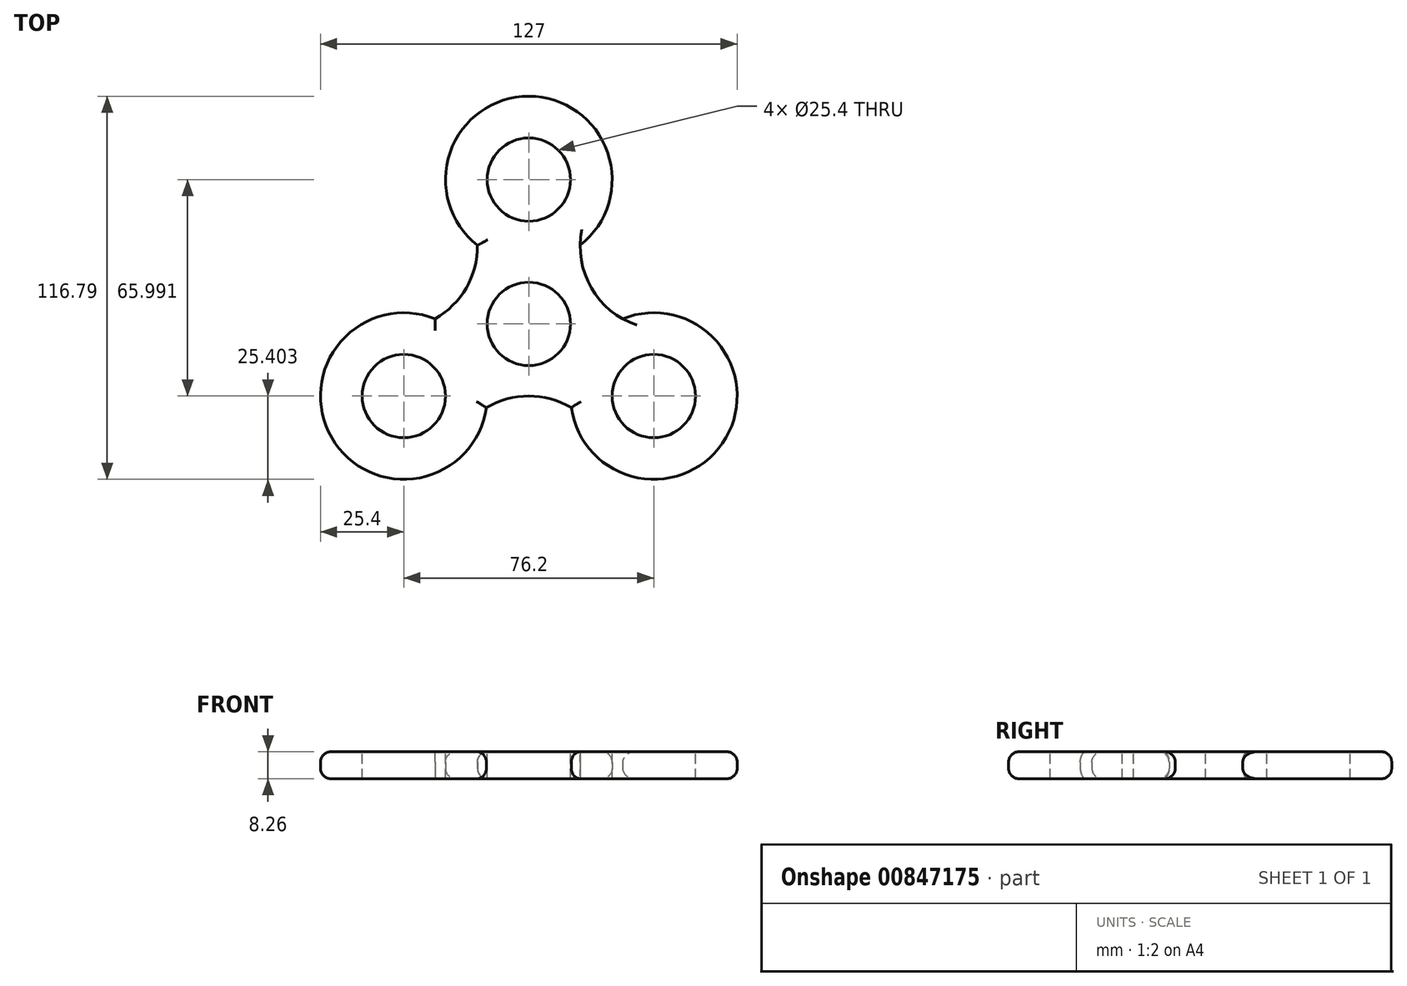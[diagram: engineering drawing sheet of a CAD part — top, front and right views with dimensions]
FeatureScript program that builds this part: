
annotation { "Feature Type Name" : "Feature", "Feature Type Description" : "" }
export const myFeature = defineFeature(function(context is Context, id is Id, definition is map)
    precondition{}
    {
        {
            var Q0;
            Q0=qCreatedBy(makeId("Top.planeOp"),FACE);
            var sketch = newSketch(context, id + "F0", { "sketchPlane" : qUnion([Q0])});
            skArc(sketch, "E0", {"start": v(15.65, 23.99) * mm, "mid": v(0, 69.4) * mm, "end": v(-15.65, 23.99) * mm});
            skArc(sketch, "E1", {"start": v(12.95, -25.55) * mm, "mid": v(60.1, -34.7) * mm, "end": v(28.6, 1.56) * mm});
            skArc(sketch, "E2", {"start": v(-28.6, 1.56) * mm, "mid": v(-60.1, -34.7) * mm, "end": v(-12.95, -25.55) * mm});
            skLineSegment(sketch, "E3", {"start": v(0, 44) * mm, "end": v(-38.1, -22) * mm, "construction": true});
            skLineSegment(sketch, "E4", {"start": v(0, 44) * mm, "end": v(38.1, -22) * mm, "construction": true});
            skLineSegment(sketch, "E5", {"start": v(-38.1, -22) * mm, "end": v(38.1, -22) * mm, "construction": true});
            skLineSegment(sketch, "E6", {"start": v(0, 94.8) * mm, "end": v(-82.1, -47.4) * mm, "construction": true});
            skLineSegment(sketch, "E7", {"start": v(-82.1, -47.4) * mm, "end": v(82.1, -47.4) * mm, "construction": true});
            skLineSegment(sketch, "E8", {"start": v(82.1, -47.4) * mm, "end": v(0, 94.8) * mm, "construction": true});
            skArc(sketch, "E9", {"start": v(-28.6, 1.56) * mm, "mid": v(-19.05, 11) * mm, "end": v(-15.65, 23.99) * mm});
            skArc(sketch, "E10", {"start": v(12.95, -25.55) * mm, "mid": v(0, -22) * mm, "end": v(-12.95, -25.55) * mm});
            skArc(sketch, "E11", {"start": v(15.65, 23.99) * mm, "mid": v(19.05, 11) * mm, "end": v(28.6, 1.56) * mm});
            skLineSegment(sketch, "E12", {"start": v(0, 44) * mm, "end": v(0, -22) * mm, "construction": true});
            skLineSegment(sketch, "E13", {"start": v(38.1, -22) * mm, "end": v(-19.05, 11) * mm, "construction": true});
            skLineSegment(sketch, "E14", {"start": v(-38.1, -22) * mm, "end": v(19.05, 11) * mm, "construction": true});
            skPoint(sketch, "E15", {"position": v(0, 0) * mm});
            skSolve(sketch);
        }
        {
            var Q0;
            Q0 = qSketchRegion(id + "F0", true);
            extrude(context, id + "F1", {"entities" : qUnion([Q0]), "depth" : 8.25 * mm, "offsetDistance" : 25 * mm});
        }
        {
            var Q0;
            Q0=makeQuery(id+"F1.opExtrude","CAP_EDGE",EDGE,{"disambiguationData":[OSD([sQuery(id+"F0.wireOp",EDGE,"bNZ3Z0CN-ohr7-q4Bt-xrt1-HDOuBhinMZCx")])],"isStart":true});
            var Q1;
            Q1=makeQuery(id+"F1.opExtrude","CAP_EDGE",EDGE,{"disambiguationData":[OSD([sQuery(id+"F0.wireOp",EDGE,"E0")])],"isStart":true});
            var Q2;
            Q2=makeQuery(id+"F1.opExtrude","CAP_EDGE",EDGE,{"disambiguationData":[OSD([sQuery(id+"F0.wireOp",EDGE,"E9")])],"isStart":true});
            var Q3;
            Q3=makeQuery(id+"F1.opExtrude","CAP_EDGE",EDGE,{"disambiguationData":[OSD([sQuery(id+"F0.wireOp",EDGE,"E2")])],"isStart":true});
            var Q4;
            Q4=makeQuery(id+"F1.opExtrude","CAP_EDGE",EDGE,{"disambiguationData":[OSD([sQuery(id+"F0.wireOp",EDGE,"E10")])],"isStart":true});
            var Q5;
            Q5=makeQuery(id+"F1.opExtrude","CAP_EDGE",EDGE,{"disambiguationData":[OSD([sQuery(id+"F0.wireOp",EDGE,"E1")])],"isStart":true});
            var Q6;
            Q6=makeQuery(id+"F1.opExtrude","CAP_EDGE",EDGE,{"disambiguationData":[OSD([sQuery(id+"F0.wireOp",EDGE,"E1")])],"isStart":false});
            var Q7;
            Q7=makeQuery(id+"F1.opExtrude","CAP_EDGE",EDGE,{"disambiguationData":[OSD([sQuery(id+"F0.wireOp",EDGE,"bNZ3Z0CN-ohr7-q4Bt-xrt1-HDOuBhinMZCx")])],"isStart":false});
            var Q8;
            Q8=makeQuery(id+"F1.opExtrude","CAP_EDGE",EDGE,{"disambiguationData":[OSD([sQuery(id+"F0.wireOp",EDGE,"E0")])],"isStart":false});
            var Q9;
            Q9=makeQuery(id+"F1.opExtrude","CAP_EDGE",EDGE,{"disambiguationData":[OSD([sQuery(id+"F0.wireOp",EDGE,"E9")])],"isStart":false});
            var Q10;
            Q10=makeQuery(id+"F1.opExtrude","CAP_EDGE",EDGE,{"disambiguationData":[OSD([sQuery(id+"F0.wireOp",EDGE,"E2")])],"isStart":false});
            var Q11;
            Q11=makeQuery(id+"F1.opExtrude","CAP_EDGE",EDGE,{"disambiguationData":[OSD([sQuery(id+"F0.wireOp",EDGE,"E10")])],"isStart":false});
            fillet(context, id + "F2", {"entities" : qUnion([Q0, Q1, Q2, Q3, Q4, Q5, Q6, Q7, Q8, Q9, Q10, Q11]), "radius" : 3.17 * mm, "tangentPropagation" : true, "allowEdgeOverflow" : false});
        }
        {
            var Q0;
            Q0=makeQuery(id+"F1.opExtrude","CAP_FACE",FACE,{"disambiguationData":[OSD([sQuery(id+"F0.wireOp",EDGE,"E0"),sQuery(id+"F0.wireOp",EDGE,"E1"),sQuery(id+"F0.wireOp",EDGE,"E2"),sQuery(id+"F0.wireOp",EDGE,"E9"),sQuery(id+"F0.wireOp",EDGE,"bNZ3Z0CN-ohr7-q4Bt-xrt1-HDOuBhinMZCx"),sQuery(id+"F0.wireOp",EDGE,"E10")])],"isStart":false});
            var sketch = newSketch(context, id + "F3", { "sketchPlane" : qUnion([Q0])});
            skPoint(sketch, "E16", {"position": v(0, 44) * mm});
            skPoint(sketch, "E17", {"position": v(-38.1, -22) * mm});
            skPoint(sketch, "E18", {"position": v(38.1, -22) * mm});
            skPoint(sketch, "E19", {"position": v(0, 0) * mm});
            skSolve(sketch);
        }
        {
            var Q0;
            Q0=sQuery(id+"F3.wireOp",VERTEX,"E16");
            var Q1;
            Q1=sQuery(id+"F3.wireOp",VERTEX,"E17");
            var Q2;
            Q2=sQuery(id+"F3.wireOp",VERTEX,"E18");
            var Q3;
            Q3=sQuery(id+"F3.wireOp",VERTEX,"E19");
            var Q4;
            Q4=makeQuery(id+"F1.opExtrude","SWEPT_BODY",BODY,{"disambiguationData":[OSD([sQuery(id+"F0.wireOp",EDGE,"E0"),sQuery(id+"F0.wireOp",EDGE,"E1"),sQuery(id+"F0.wireOp",EDGE,"E2"),sQuery(id+"F0.wireOp",EDGE,"E9"),sQuery(id+"F0.wireOp",EDGE,"bNZ3Z0CN-ohr7-q4Bt-xrt1-HDOuBhinMZCx"),sQuery(id+"F0.wireOp",EDGE,"E10")])]});
            hole(context, id + "F4", {"style" : HoleStyle.SIMPLE, "endStyle" : HoleEndStyle.BLIND, "holeDiameter" : 25.4 * mm, "majorDiameter" : 5 * mm, "holeDepth" : 8.25 * mm, "isTappedThrough" : true, "tappedDepth" : 12 * mm, "tapClearance" : 3, "locations" : qUnion([Q0, Q1, Q2, Q3]), "scope" : qUnion([Q4])});
        }
    });
